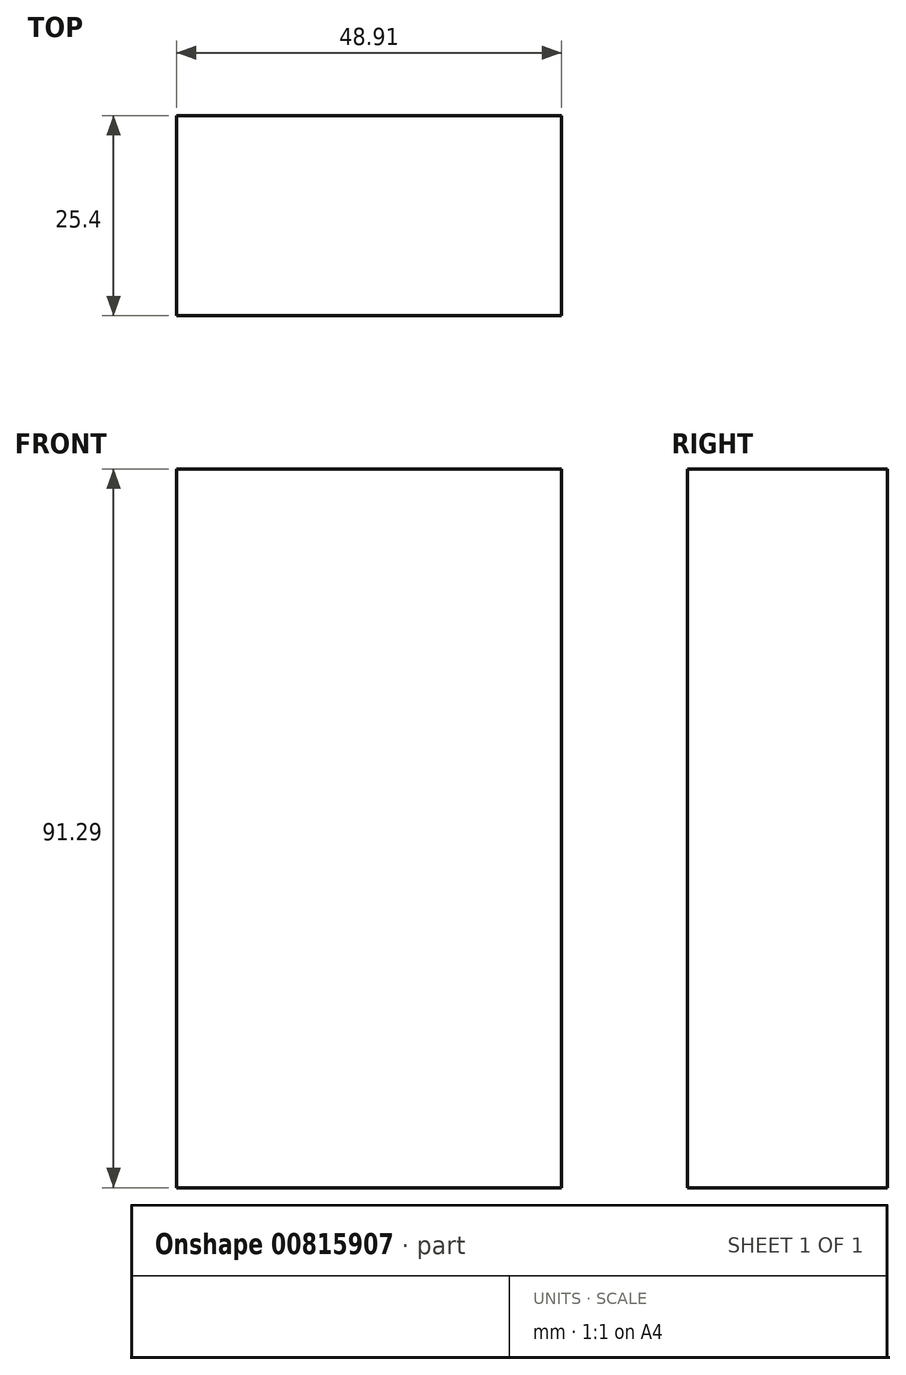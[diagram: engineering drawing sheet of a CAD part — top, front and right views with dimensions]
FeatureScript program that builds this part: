
annotation { "Feature Type Name" : "Feature", "Feature Type Description" : "" }
export const myFeature = defineFeature(function(context is Context, id is Id, definition is map)
    precondition{}
    {
        {
            var Q0;
            Q0=qCreatedBy(makeId("Front.planeOp"),FACE);
            var sketch = newSketch(context, id + "F0", { "sketchPlane" : qUnion([Q0])});
            skArc(sketch, "E0", {"start": v(-61.3, -38.06) * mm, "mid": v(47.26, -37.48) * mm, "end": v(-12.4, 53.23) * mm});
            skLineSegment(sketch, "E1.bottom", {"start": v(-61.3, -38.06) * mm, "end": v(-12.4, -38.06) * mm});
            skLineSegment(sketch, "E1.top", {"start": v(-61.3, 53.23) * mm, "end": v(-12.4, 53.23) * mm});
            skLineSegment(sketch, "E1.left", {"start": v(-61.3, -38.06) * mm, "end": v(-61.3, 53.23) * mm});
            skLineSegment(sketch, "E1.right", {"start": v(-12.4, -38.06) * mm, "end": v(-12.4, 53.23) * mm});
            skSolve(sketch);
        }
        {
            var Q0;
            Q0=makeQuery(id+"F0.imprint","IMPRINT",FACE,{"disambiguationData":[TD([[makeQuery(id+"F0.imprint","IMPRINT",EDGE,{"derivedFrom":sQuery(id+"F0.wireOp",EDGE,"E1.bottom")}),1.0]])]});
            extrude(context, id + "F1", {"entities" : qUnion([Q0]), "depth" : 25.4 * mm, "offsetDistance" : 25.4 * mm});
        }
    });
